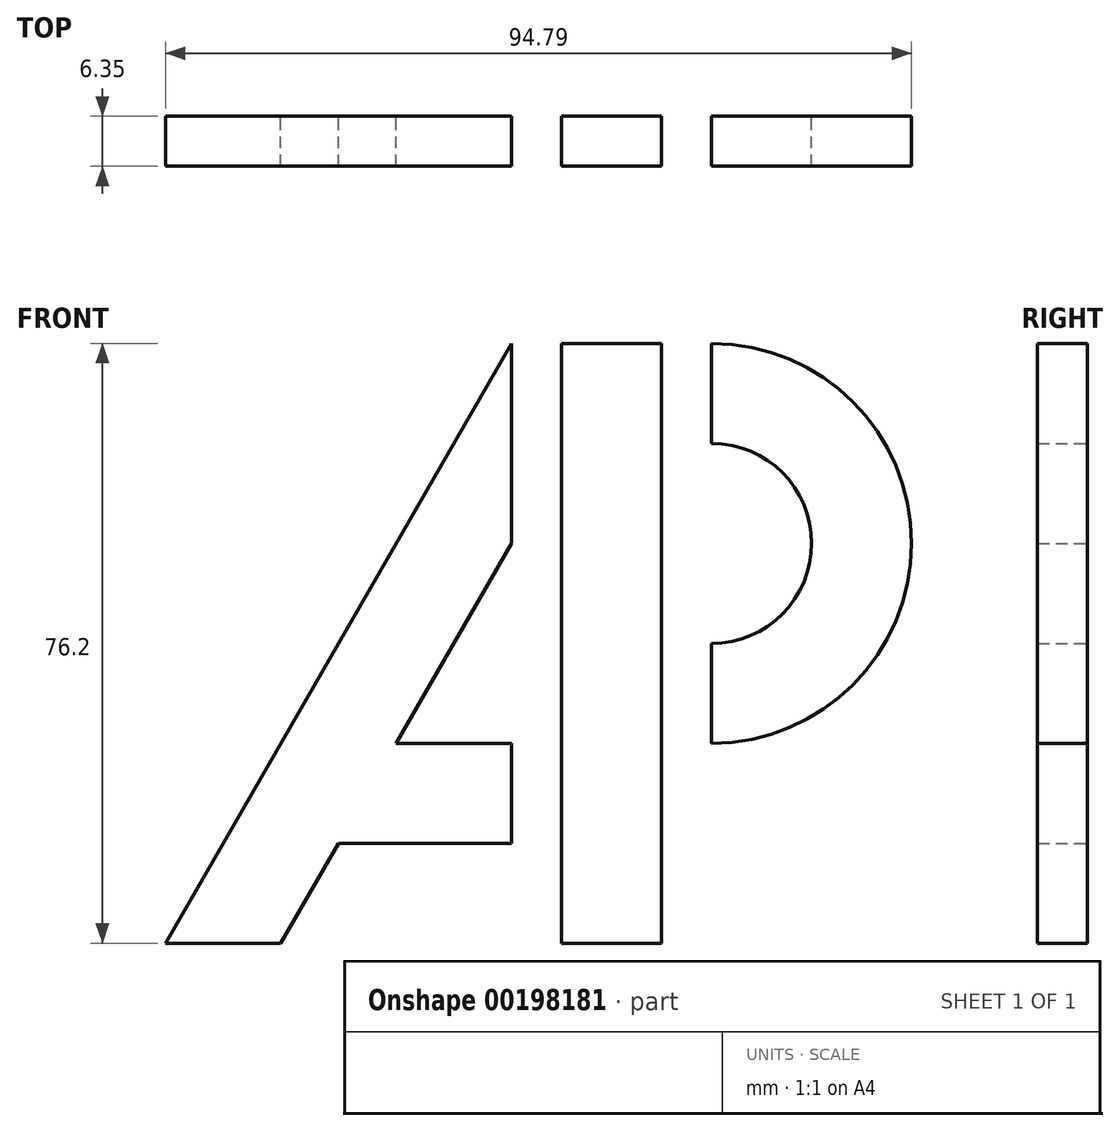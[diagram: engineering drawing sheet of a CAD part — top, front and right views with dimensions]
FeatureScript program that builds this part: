
annotation { "Feature Type Name" : "Feature", "Feature Type Description" : "" }
export const myFeature = defineFeature(function(context is Context, id is Id, definition is map)
    precondition{}
    {
        {
            var Q0;
            Q0=qCreatedBy(makeId("Front.planeOp"),FACE);
            var sketch = newSketch(context, id + "F0", { "sketchPlane" : qUnion([Q0])});
            skLineSegment(sketch, "E0.bottom", {"start": v(-6.35, 38.1) * mm, "end": v(6.35, 38.1) * mm});
            skLineSegment(sketch, "E0.top", {"start": v(-6.35, -38.1) * mm, "end": v(6.35, -38.1) * mm});
            skLineSegment(sketch, "E0.left", {"start": v(-6.35, 38.1) * mm, "end": v(-6.35, -38.1) * mm});
            skLineSegment(sketch, "E0.right", {"start": v(6.35, 38.1) * mm, "end": v(6.35, -38.1) * mm});
            skPoint(sketch, "E0.middle", {"position": v(0, 0) * mm});
            skLineSegment(sketch, "E1.bottom", {"start": v(6.35, 38.1) * mm, "end": v(12.7, 38.1) * mm});
            skLineSegment(sketch, "E1.top", {"start": v(6.35, 25.4) * mm, "end": v(12.7, 25.4) * mm});
            skLineSegment(sketch, "E1.left", {"start": v(6.35, 38.1) * mm, "end": v(6.35, 25.4) * mm});
            skLineSegment(sketch, "E1.right", {"start": v(12.7, 38.1) * mm, "end": v(12.7, 25.4) * mm});
            skLineSegment(sketch, "E2.bottom", {"start": v(6.35, 0) * mm, "end": v(12.7, 0) * mm});
            skLineSegment(sketch, "E2.top", {"start": v(6.35, -12.7) * mm, "end": v(12.7, -12.7) * mm});
            skLineSegment(sketch, "E2.left", {"start": v(6.35, 0) * mm, "end": v(6.35, -12.7) * mm});
            skLineSegment(sketch, "E2.right", {"start": v(12.7, 0) * mm, "end": v(12.7, -12.7) * mm});
            skLineSegment(sketch, "E3.bottom", {"start": v(-6.35, 38.1) * mm, "end": v(-12.7, 38.1) * mm});
            skLineSegment(sketch, "E3.top", {"start": v(-6.35, 12.7) * mm, "end": v(-12.7, 12.7) * mm});
            skLineSegment(sketch, "E3.left", {"start": v(-6.35, 38.1) * mm, "end": v(-6.35, 12.7) * mm});
            skLineSegment(sketch, "E3.right", {"start": v(-12.7, 38.1) * mm, "end": v(-12.7, 12.7) * mm});
            skLineSegment(sketch, "E4.bottom", {"start": v(-6.35, -38.1) * mm, "end": v(-12.7, -38.1) * mm});
            skLineSegment(sketch, "E4.top", {"start": v(-6.35, -25.4) * mm, "end": v(-12.7, -25.4) * mm});
            skLineSegment(sketch, "E4.left", {"start": v(-6.35, -38.1) * mm, "end": v(-6.35, -25.4) * mm});
            skLineSegment(sketch, "E4.right", {"start": v(-12.7, -38.1) * mm, "end": v(-12.7, -25.4) * mm});
            skArc(sketch, "E5", {"start": v(12.7, 0) * mm, "mid": v(25.4, 12.7) * mm, "end": v(12.7, 25.4) * mm});
            skArc(sketch, "E6", {"start": v(12.7, -12.7) * mm, "mid": v(38.1, 12.7) * mm, "end": v(12.7, 38.1) * mm});
            skLineSegment(sketch, "E7", {"start": v(-12.7, -38.1) * mm, "end": v(-56.7, -38.1) * mm});
            skLineSegment(sketch, "E8", {"start": v(-56.7, -38.1) * mm, "end": v(-12.7, 38.1) * mm});
            skLineSegment(sketch, "E9", {"start": v(-12.7, 12.7) * mm, "end": v(-34.7, -25.4) * mm});
            skLineSegment(sketch, "E10", {"start": v(-34.7, -25.4) * mm, "end": v(-12.7, -25.4) * mm});
            skLineSegment(sketch, "E11", {"start": v(-12.7, -25.4) * mm, "end": v(-12.7, -12.7) * mm});
            skLineSegment(sketch, "E12", {"start": v(-12.7, -12.7) * mm, "end": v(-6.35, -12.7) * mm});
            skLineSegment(sketch, "E13", {"start": v(-12.7, -12.7) * mm, "end": v(-27.36, -12.7) * mm});
            skLineSegment(sketch, "E14", {"start": v(-34.7, -25.4) * mm, "end": v(-42.03, -38.1) * mm});
            skSolve(sketch);
        }
        {
            var Q0;
            Q0=makeQuery(id+"F0.imprint","IMPRINT",FACE,{"disambiguationData":[TD([[makeQuery(id+"F0.imprint","IMPRINT",EDGE,{"derivedFrom":sQuery(id+"F0.wireOp",EDGE,"E3.right")}),-1.0]])]});
            var Q1;
            Q1=makeQuery(id+"F0.imprint","IMPRINT",FACE,{"disambiguationData":[TD([[makeQuery(id+"F0.imprint","IMPRINT",EDGE,{"derivedFrom":sQuery(id+"F0.wireOp",EDGE,"E0.bottom")}),-1.0]])]});
            var Q2;
            Q2=makeQuery(id+"F0.imprint","IMPRINT",FACE,{"disambiguationData":[TD([[makeQuery(id+"F0.imprint","IMPRINT",EDGE,{"derivedFrom":sQuery(id+"F0.wireOp",EDGE,"E1.right")}),1.0]])]});
            var Q3;
            {var subQ0=sQuery(id+"F0.wireOp",EDGE,"E10");Q3=makeQuery(id+"F0.imprint","IMPRINT",FACE,{"disambiguationData":[TD([[makeQuery(id+"F0.imprint","IMPRINT",EDGE,{"derivedFrom":subQ0}),1.0]])]});}
            extrude(context, id + "F1", {"entities" : qUnion([Q0, Q1, Q2, Q3]), "depth" : 6.35 * mm});
        }
    });
